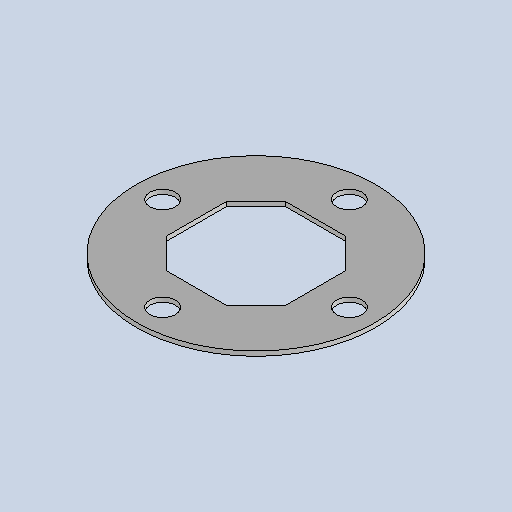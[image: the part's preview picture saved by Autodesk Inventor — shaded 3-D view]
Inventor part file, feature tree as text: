
AUTODESK INVENTOR PART (.ipt)
format: ipt  version: 2025.3 (Build 293356030, 356C)  size: 207,360 bytes
history: native  units: mm
features: other x3, sketch x2, sheet_metal_op x1
ambient origin geometry x8: Origin, YZ Plane, XZ Plane, XY Plane, X Axis, Y Axis, Z Axis, Center Point
bodies: Body1 (feature_tree)
feature tree (6):
  sheet_metal_op  "Face3"
  other  "Corner Chamfer2"
  sketch  "Sketch1"  dims[d61=500.0mm]
  other  "Plate5"
  sketch  "Sketch Circular Pattern1"  dims[d156=3.0mm d157=160.0mm d158=80.0mm d159=80.0mm d167=20.0mm d168=6.0mm d169=45.0deg d170=17.0mm d171=125.0mm d172=40.0mm d174=360.0deg]
  other  "Definition1"
